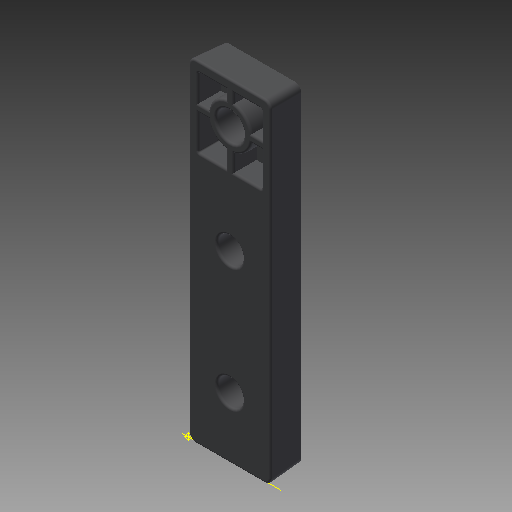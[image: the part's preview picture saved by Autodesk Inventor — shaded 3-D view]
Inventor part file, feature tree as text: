
AUTODESK INVENTOR PART (.ipt)
format: ipt  version: 2018 (Build 220112000, 112)  size: 470,016 bytes
history: native  units: in
note: dims shown in document units (in); Inventor stores cm internally (conversion verified against a paired STEP export)
features: sketch x12, extrude x10, fillet x7, projected_geometry x5, hole x2, plane x2, mirror x1, pattern_linear x1, other x1
ambient origin geometry x8: Origin, YZ Plane, XZ Plane, XY Plane, X Axis, Y Axis, Z Axis, Center Point
bodies: Solid1 (feature_tree)
feature tree (41):
  extrude  "Extrusion1"  Depth=2.026in
  hole  "Hole1"  [1 undecoded]
  extrude  "Extrusion2"  Depth=0.014in
  fillet  "Fillet1"  Radius=0.014in
  extrude  "Extrusion3"  Depth=0.02in
  extrude  "Extrusion4"  Depth=0.027in
  extrude  "Extrusion5"  Depth=0.028in
  extrude  "Extrusion7"  Depth=0.03in
  extrude  "Extrusion8"  Depth=0.03in
  fillet  "Fillet2"  Radius=0.008in
  plane  "Work Plane1"
  mirror  "Mirror1"
  pattern_linear  "Rectangular Pattern2"  Spacing1=0.228in  [1 undecoded]
  fillet  "Fillet3"  Radius=0.228in
  extrude  "Extrusion9"  Depth=0.031in
  hole  "Hole2"  [1 undecoded]
  extrude  "Extrusion10"  Depth=0.031in
  fillet  "Fillet4"  Radius=0.224in
  fillet  "Fillet5"  Radius=0.002in
  fillet  "Fillet6"  Radius=0.047in
  plane  "Work Plane4"
  extrude  "Extrusion11"  Depth=0.031in
  fillet  "Fillet7"  Radius=0.014in
  sketch  "Sketch1"  dims[d3=0.5in d4=2.026in]
  sketch  "Sketch2"  dims[d6=0.197in d7=-0.0206in d8=0.25in]
  sketch  "Sketch3"  dims[d9=0.25in]
  sketch  "Sketch4"  dims[d10=0.171in d11=0.75in d12=0.375in d13=0.25in d14=0.5635in d15=1.0in d16=0.8108in d17=0.138in d18=-0.0069in d19=0.014in]
  sketch  "Sketch5"  dims[d20=0.027in d21=0.02in]
  sketch  "Sketch6"  dims[d22=0.027in d23=0.027in]
  sketch  "Sketch7"  dims[d24=1.479in d25=0.028in d26=-0.0034in]
  projected_geometry  "Projected Loop1"
  sketch  "Sketch8"  dims[d28=0.03in d29=0.03in]
  sketch  "Sketch9"  dims[d30=0.03in d31=0.03in d32=0.008in]
  projected_geometry  "Projected Loop2"
  sketch  "Sketch10"  dims[d33=0.11in d34=-0.0034in]
  projected_geometry  "Projected Loop3"
  sketch  "Sketch11"  dims[d35=0.656in]
  other  "Work Axis1"
  sketch  "Sketch14"  dims[d36=0.748in d37=0.228in d38=0.228in d39=0.224in d40=-0.0069in d41=0.037in d42=0.0185in d45=0.224in d46=0.0034in d47=0.002in d48=0.047in d49=0.0034in d50=0.012in d54=0.014in d55=0.122in d56=0.122in d57=0.039in d58=-0.0069in d59=0.083in d60=0.75in d61=0.375in d62=0.25in d63=0.5635in d64=1.0in d65=0.8108in d66=0.157in d67=0.224in d68=0.0in d69=0.014in d70=0.012in d71=0.7874in d73=0.748in d74=0.039in d75=90.0deg d76=0.028in d77=0.197in d78=1.0in d79=0.0in d80=0.031in]
  projected_geometry  "Projected Loop4"
  projected_geometry  "Project Cut Edges3"
note: 3 required parameter values undecoded (feature->parameter linkage not recoverable at this tier; creation-order binding heuristic only, values carry confidence <= 0.55)
